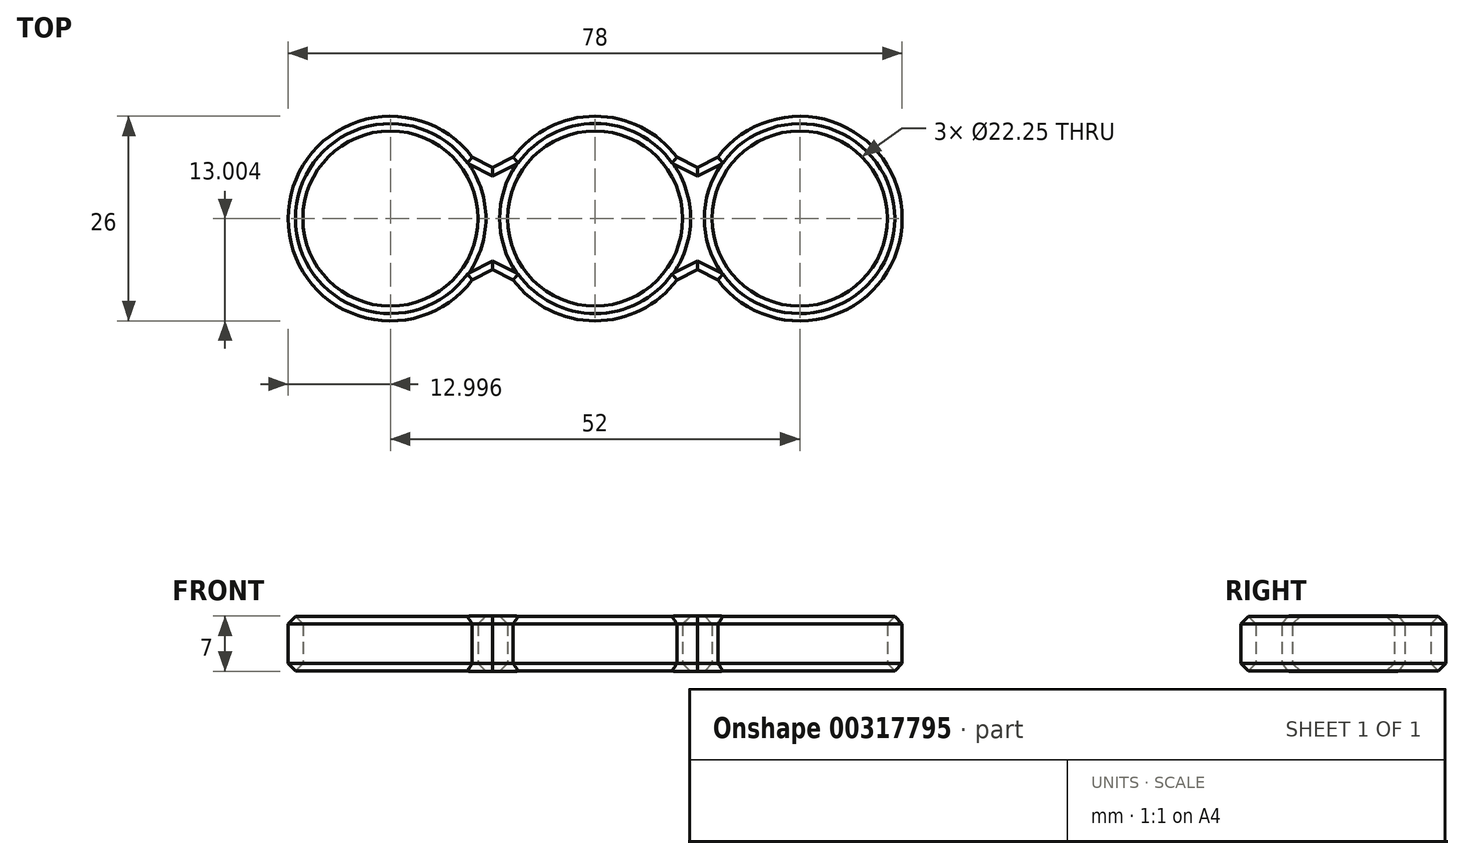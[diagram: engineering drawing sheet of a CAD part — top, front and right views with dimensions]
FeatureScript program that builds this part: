
annotation { "Feature Type Name" : "Feature", "Feature Type Description" : "" }
export const myFeature = defineFeature(function(context is Context, id is Id, definition is map)
    precondition{}
    {
        {
            var Q0;
            Q0=qCreatedBy(makeId("Top.planeOp"),FACE);
            var sketch = newSketch(context, id + "F0", { "sketchPlane" : qUnion([Q0])});
            skCircle(sketch, "E0", {"center": v(-26.5, 3.33) * mm, "radius": 11.12 * mm});
            skCircle(sketch, "E1", {"center": v(-0.5, 3.33) * mm, "radius": 11.12 * mm});
            skCircle(sketch, "E2", {"center": v(-52.5, 3.33) * mm, "radius": 11.12 * mm});
            skCircle(sketch, "E3", {"center": v(-52.5, 3.33) * mm, "radius": 13 * mm});
            skCircle(sketch, "E4", {"center": v(-26.5, 3.33) * mm, "radius": 13 * mm});
            skCircle(sketch, "E5", {"center": v(-0.5, 3.33) * mm, "radius": 13 * mm});
            skLineSegment(sketch, "E6", {"start": v(-26.5, 16.33) * mm, "end": v(-52.5, 3.33) * mm, "construction": true});
            skLineSegment(sketch, "E7", {"start": v(-26.5, 16.33) * mm, "end": v(-39.5, 9.83) * mm});
            skLineSegment(sketch, "E8", {"start": v(-39.5, 9.83) * mm, "end": v(-52.5, 16.33) * mm});
            skLineSegment(sketch, "E9", {"start": v(-52.5, -9.67) * mm, "end": v(-39.5, -3.17) * mm});
            skLineSegment(sketch, "E10", {"start": v(-39.5, -3.17) * mm, "end": v(-26.5, -9.67) * mm});
            skLineSegment(sketch, "E11", {"start": v(-26.5, -9.67) * mm, "end": v(-13.5, -3.17) * mm});
            skLineSegment(sketch, "E12", {"start": v(-13.5, -3.17) * mm, "end": v(-0.5, -9.67) * mm});
            skLineSegment(sketch, "E13", {"start": v(-26.5, 16.33) * mm, "end": v(-13.5, 9.83) * mm});
            skLineSegment(sketch, "E14", {"start": v(-13.5, 9.83) * mm, "end": v(-0.5, 16.33) * mm});
            skSolve(sketch);
        }
        {
            var Q0;
            Q0 = qSketchRegion(id + "F0", true);
            extrude(context, id + "F1", {"entities" : qUnion([Q0]), "depth" : 7 * mm});
        }
        {
            var Q0;
            Q0=makeQuery(id+"F1.opExtrude","CAP_FACE",FACE,{"disambiguationData":[OSD([sQuery(id+"F0.wireOp",EDGE,"E0"),sQuery(id+"F0.wireOp",EDGE,"E1"),sQuery(id+"F0.wireOp",EDGE,"E2"),sQuery(id+"F0.wireOp",EDGE,"E3"),sQuery(id+"F0.wireOp",EDGE,"E4"),sQuery(id+"F0.wireOp",EDGE,"E5"),sQuery(id+"F0.wireOp",EDGE,"E7"),sQuery(id+"F0.wireOp",EDGE,"E8"),sQuery(id+"F0.wireOp",EDGE,"E9"),sQuery(id+"F0.wireOp",EDGE,"E10"),sQuery(id+"F0.wireOp",EDGE,"E11"),sQuery(id+"F0.wireOp",EDGE,"E12"),sQuery(id+"F0.wireOp",EDGE,"E13"),sQuery(id+"F0.wireOp",EDGE,"E14")])],"isStart":false});
            var Q1;
            Q1=makeQuery(id+"F1.opExtrude","CAP_FACE",FACE,{"disambiguationData":[OSD([sQuery(id+"F0.wireOp",EDGE,"E0"),sQuery(id+"F0.wireOp",EDGE,"E1"),sQuery(id+"F0.wireOp",EDGE,"E2"),sQuery(id+"F0.wireOp",EDGE,"E3"),sQuery(id+"F0.wireOp",EDGE,"E4"),sQuery(id+"F0.wireOp",EDGE,"E5"),sQuery(id+"F0.wireOp",EDGE,"E7"),sQuery(id+"F0.wireOp",EDGE,"E8"),sQuery(id+"F0.wireOp",EDGE,"E9"),sQuery(id+"F0.wireOp",EDGE,"E10"),sQuery(id+"F0.wireOp",EDGE,"E11"),sQuery(id+"F0.wireOp",EDGE,"E12"),sQuery(id+"F0.wireOp",EDGE,"E13"),sQuery(id+"F0.wireOp",EDGE,"E14")])],"isStart":true});
            chamfer(context, id + "F2", {"entities" : qUnion([Q0, Q1]), "width" : 1 * mm, "tangentPropagation" : true});
        }
    });
